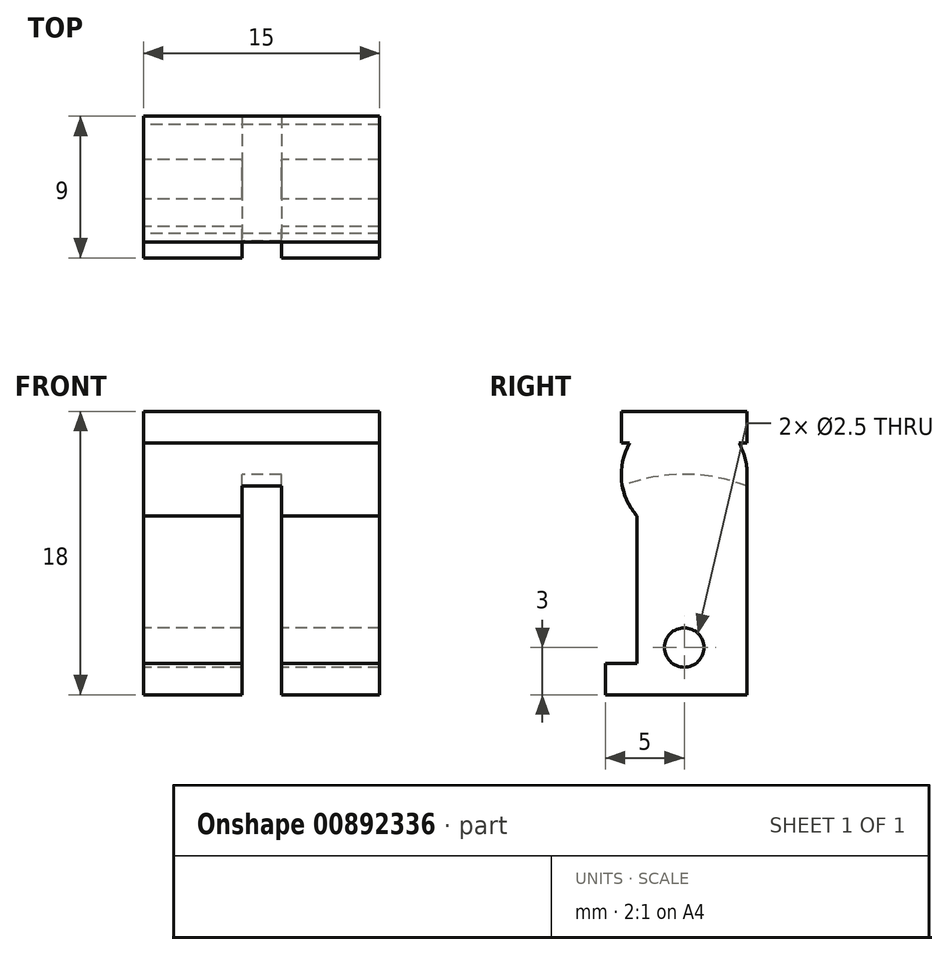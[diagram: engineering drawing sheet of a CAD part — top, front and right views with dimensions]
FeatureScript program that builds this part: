
annotation { "Feature Type Name" : "Feature", "Feature Type Description" : "" }
export const myFeature = defineFeature(function(context is Context, id is Id, definition is map)
    precondition{}
    {
        {
            var Q0;
            Q0=qCreatedBy(makeId("Right.planeOp"),FACE);
            var sketch = newSketch(context, id + "F0", { "sketchPlane" : qUnion([Q0])});
            skLineSegment(sketch, "E0.bottom", {"start": v(4, -1) * mm, "end": v(3.46, -1) * mm});
            skLineSegment(sketch, "E0.top", {"start": v(4, 1) * mm, "end": v(-4, 1) * mm});
            skLineSegment(sketch, "E0.left", {"start": v(4, -1) * mm, "end": v(4, 1) * mm});
            skLineSegment(sketch, "E0.right", {"start": v(-4, -1) * mm, "end": v(-4, 1) * mm});
            skPoint(sketch, "E0.middle", {"position": v(0, 0) * mm});
            skArc(sketch, "E1", {"start": v(-3.46, -1) * mm, "mid": v(-3.98, -3.4) * mm, "end": v(-3, -5.65) * mm});
            skPoint(sketch, "E1.centerSnap0", {"position": v(0, -1) * mm});
            skLineSegment(sketch, "E2.left", {"start": v(4, -3) * mm, "end": v(4, -15) * mm});
            skLineSegment(sketch, "E2.right", {"start": v(-3, -5.65) * mm, "end": v(-3, -15) * mm});
            skLineSegment(sketch, "E3.top", {"start": v(4, -17) * mm, "end": v(-5, -17) * mm});
            skLineSegment(sketch, "E3.left", {"start": v(4, -15) * mm, "end": v(4, -17) * mm});
            skLineSegment(sketch, "E3.right", {"start": v(-5, -15) * mm, "end": v(-5, -17) * mm});
            skCircle(sketch, "E4", {"center": v(0, -14) * mm, "radius": 1.25 * mm});
            skLineSegment(sketch, "E5.trimOffspring", {"start": v(-3.46, -1) * mm, "end": v(-4, -1) * mm});
            skArc(sketch, "E6.trimOffspring", {"start": v(4, -3) * mm, "mid": v(3.86, -1.96) * mm, "end": v(3.46, -1) * mm});
            skLineSegment(sketch, "E7.trimOffspring", {"start": v(-3, -15) * mm, "end": v(-5, -15) * mm});
            skSolve(sketch);
        }
        {
            var Q0;
            Q0 = qSketchRegion(id + "F0", true);
            extrude(context, id + "F1", {"entities" : qUnion([Q0]), "endBound" : BoundingType.SYMMETRIC, "depth" : 15 * mm, "offsetDistance" : 25.4 * mm});
        }
        {
            var Q0;
            Q0=qCreatedBy(makeId("Right.planeOp"),FACE);
            var sketch = newSketch(context, id + "F2", { "sketchPlane" : qUnion([Q0])});
            skCircle(sketch, "E8", {"center": v(0, -14) * mm, "radius": 11 * mm});
            skSolve(sketch);
        }
        {
            var Q0;
            Q0 = qSketchRegion(id + "F2", true);
            extrude(context, id + "F3", {"entities" : qUnion([Q0]), "operationType" : NewBodyOperationType.REMOVE, "endBound" : BoundingType.SYMMETRIC, "depth" : 2.5 * mm, "offsetDistance" : 25.4 * mm});
        }
    });
